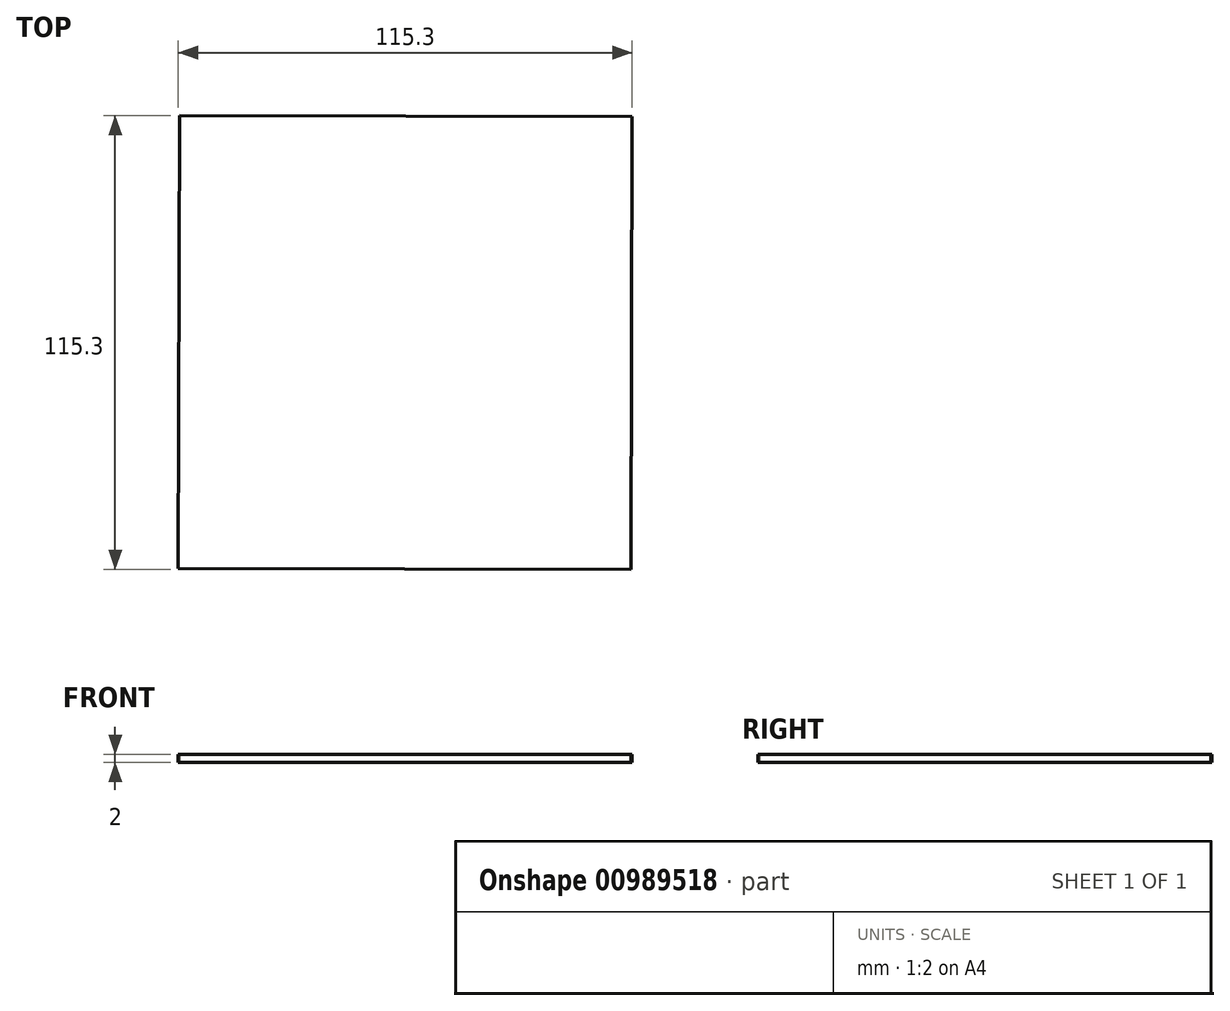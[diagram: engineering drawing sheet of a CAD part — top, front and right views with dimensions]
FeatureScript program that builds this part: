
annotation { "Feature Type Name" : "Feature", "Feature Type Description" : "" }
export const myFeature = defineFeature(function(context is Context, id is Id, definition is map)
    precondition{}
    {
        {
            var Q0;
            Q0=qCreatedBy(makeId("Top.planeOp"),FACE);
            var sketch = newSketch(context, id + "F0", { "sketchPlane" : qUnion([Q0])});
            skCircle(sketch, "E0.cCircle", {"center": v(0, 0) * mm, "radius": 57.5 * mm, "construction": true});
            skLineSegment(sketch, "E0.0", {"start": v(-57.65, -57.35) * mm, "end": v(-57.35, 57.65) * mm});
            skLineSegment(sketch, "E0.1", {"start": v(-57.35, 57.65) * mm, "end": v(57.65, 57.35) * mm});
            skLineSegment(sketch, "E0.2", {"start": v(57.65, 57.35) * mm, "end": v(57.35, -57.65) * mm});
            skLineSegment(sketch, "E0.3", {"start": v(57.35, -57.65) * mm, "end": v(-57.65, -57.35) * mm});
            skPoint(sketch, "E0.0.midPoint", {"position": v(-57.5, 0.15) * mm});
            skSolve(sketch);
        }
        {
            var Q0;
            Q0 = qSketchRegion(id + "F0", true);
            extrude(context, id + "F1", {"entities" : qUnion([Q0]), "depth" : 2 * mm, "offsetDistance" : 25 * mm});
        }
    });
